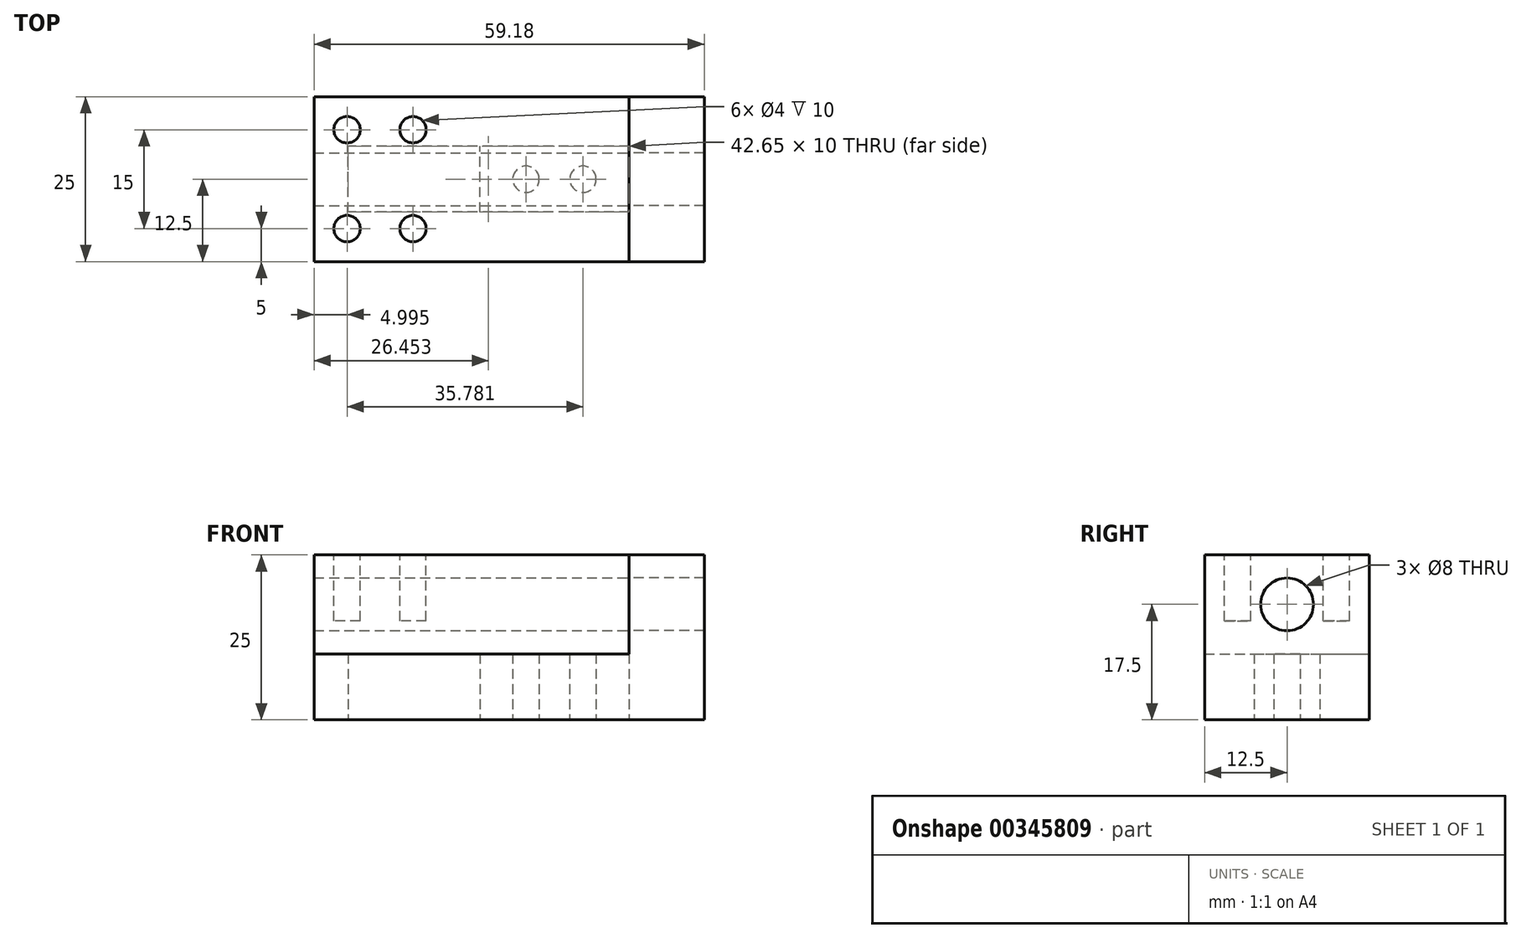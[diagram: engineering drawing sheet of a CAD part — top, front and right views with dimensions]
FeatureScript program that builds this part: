
annotation { "Feature Type Name" : "Feature", "Feature Type Description" : "" }
export const myFeature = defineFeature(function(context is Context, id is Id, definition is map)
    precondition{}
    {
        {
            var Q0;
            Q0=qCreatedBy(makeId("Top.planeOp"),FACE);
            var sketch = newSketch(context, id + "F0", { "sketchPlane" : qUnion([Q0])});
            skLineSegment(sketch, "E0.bottom", {"start": v(29.6, -12.5) * mm, "end": v(-29.6, -12.5) * mm});
            skLineSegment(sketch, "E0.top", {"start": v(29.6, 12.5) * mm, "end": v(-29.6, 12.5) * mm});
            skLineSegment(sketch, "E0.left", {"start": v(29.6, -12.5) * mm, "end": v(29.6, 12.5) * mm});
            skLineSegment(sketch, "E0.right", {"start": v(-29.6, -12.5) * mm, "end": v(-29.6, 12.5) * mm});
            skPoint(sketch, "E0.middle", {"position": v(0, 0) * mm});
            skLineSegment(sketch, "E1.bottom", {"start": v(24.46, -5) * mm, "end": v(-24.46, -5) * mm});
            skLineSegment(sketch, "E1.top", {"start": v(24.46, 5) * mm, "end": v(-24.46, 5) * mm});
            skLineSegment(sketch, "E1.left", {"start": v(24.46, -5) * mm, "end": v(24.46, 5) * mm});
            skLineSegment(sketch, "E1.right", {"start": v(-24.46, -5) * mm, "end": v(-24.46, 5) * mm});
            skSolve(sketch);
        }
        {
            var Q0;
            Q0 = qSketchRegion(id + "F0", true);
            extrude(context, id + "F1", {"entities" : qUnion([Q0]), "depth" : 10 * mm});
        }
        {
            var Q0;
            Q0=makeQuery(id+"F1.opExtrude","CAP_FACE",FACE,{"disambiguationData":[OSD([sQuery(id+"F0.wireOp",EDGE,"E0.bottom"),sQuery(id+"F0.wireOp",EDGE,"E0.top"),sQuery(id+"F0.wireOp",EDGE,"E0.left"),sQuery(id+"F0.wireOp",EDGE,"E0.right"),sQuery(id+"F0.wireOp",EDGE,"E1.bottom"),sQuery(id+"F0.wireOp",EDGE,"E1.top"),sQuery(id+"F0.wireOp",EDGE,"E1.left"),sQuery(id+"F0.wireOp",EDGE,"E1.right")])],"isStart":false});
            var sketch = newSketch(context, id + "F2", { "sketchPlane" : qUnion([Q0])});
            skLineSegment(sketch, "E2.bottom", {"start": v(29.6, -12.5) * mm, "end": v(18.19, -12.5) * mm});
            skLineSegment(sketch, "E2.top", {"start": v(29.6, 12.5) * mm, "end": v(18.19, 12.5) * mm});
            skLineSegment(sketch, "E2.left", {"start": v(29.6, -12.5) * mm, "end": v(29.6, 12.5) * mm});
            skLineSegment(sketch, "E2.right", {"start": v(18.19, -12.5) * mm, "end": v(18.19, 12.5) * mm});
            skSolve(sketch);
        }
        {
            var Q0;
            Q0 = qSketchRegion(id + "F2", true);
            extrude(context, id + "F3", {"entities" : qUnion([Q0]), "operationType" : NewBodyOperationType.ADD, "depth" : 15 * mm});
        }
        {
            var Q0;
            Q0 = qSketchRegion(id + "F2", true);
            extrude(context, id + "F4", {"entities" : qUnion([Q0]), "operationType" : NewBodyOperationType.ADD, "oppositeDirection" : true, "depth" : 10 * mm});
        }
        {
            var Q0;
            {var subQ0=sQuery(id+"F2.wireOp",EDGE,"E2.right");Q0=makeQuery(id+"F4.boolean.opBoolean","MERGE",FACE,{"derivedFrom":[makeQuery(id+"F3.opExtrude","SWEPT_FACE",FACE,{"disambiguationData":[OSD([subQ0])]}),makeQuery(id+"F4.opExtrude","SWEPT_FACE",FACE,{"disambiguationData":[OSD([subQ0])]})]});}
            var sketch = newSketch(context, id + "F5", { "sketchPlane" : qUnion([Q0])});
            skLineSegment(sketch, "E3", {"start": v(-12.5, 10) * mm, "end": v(12.5, 25) * mm, "construction": true});
            skCircle(sketch, "E4", {"center": v(0, 17.5) * mm, "radius": 4 * mm});
            skSolve(sketch);
        }
        {
            var Q0;
            Q0 = qSketchRegion(id + "F5", true);
            extrude(context, id + "F6", {"entities" : qUnion([Q0]), "operationType" : NewBodyOperationType.REMOVE, "oppositeDirection" : true, "depth" : 25 * mm});
        }
        {
            var Q0;
            Q0=makeQuery(id+"F1.opExtrude","SWEPT_BODY",BODY,{"disambiguationData":[OSD([sQuery(id+"F0.wireOp",EDGE,"E0.bottom"),sQuery(id+"F0.wireOp",EDGE,"E0.top"),sQuery(id+"F0.wireOp",EDGE,"E0.left"),sQuery(id+"F0.wireOp",EDGE,"E0.right"),sQuery(id+"F0.wireOp",EDGE,"E1.bottom"),sQuery(id+"F0.wireOp",EDGE,"E1.top"),sQuery(id+"F0.wireOp",EDGE,"E1.left"),sQuery(id+"F0.wireOp",EDGE,"E1.right")])]});
            transform(context, id + "F7", {"entities" : qUnion([Q0]), "transformType" : TransformType.TRANSLATION_3D, "dx" : 0 * mm, "dy" : 0 * mm, "dz" : 0 * mm, "makeCopy" : true});
        }
        {
            var Q0;
            Q0=makeQuery(id+"F7.opPattern","COPY",FACE,{"derivedFrom":makeQuery(id+"F4.boolean.opBoolean","MERGE",FACE,{"derivedFrom":[makeQuery(id+"F1.opExtrude","CAP_FACE",FACE,{"disambiguationData":[OSD([sQuery(id+"F0.wireOp",EDGE,"E0.bottom"),sQuery(id+"F0.wireOp",EDGE,"E0.top"),sQuery(id+"F0.wireOp",EDGE,"E0.left"),sQuery(id+"F0.wireOp",EDGE,"E0.right"),sQuery(id+"F0.wireOp",EDGE,"E1.bottom"),sQuery(id+"F0.wireOp",EDGE,"E1.top"),sQuery(id+"F0.wireOp",EDGE,"E1.left"),sQuery(id+"F0.wireOp",EDGE,"E1.right")])],"isStart":true}),makeQuery(id+"F4.opExtrude","CAP_FACE",FACE,{"disambiguationData":[OSD([sQuery(id+"F2.wireOp",EDGE,"E2.bottom"),sQuery(id+"F2.wireOp",EDGE,"E2.top"),sQuery(id+"F2.wireOp",EDGE,"E2.left"),sQuery(id+"F2.wireOp",EDGE,"E2.right")])],"isStart":false})]}),"instanceName":"1"});
            var sketch = newSketch(context, id + "F8", { "sketchPlane" : qUnion([Q0])});
            skLineSegment(sketch, "E5.bottom", {"start": v(-24.46, -5) * mm, "end": v(18.19, -5) * mm});
            skLineSegment(sketch, "E5.top", {"start": v(-24.46, 5) * mm, "end": v(18.19, 5) * mm});
            skLineSegment(sketch, "E5.left", {"start": v(-24.46, -5) * mm, "end": v(-24.46, 5) * mm});
            skLineSegment(sketch, "E5.right", {"start": v(18.19, -5) * mm, "end": v(18.19, 5) * mm});
            skSolve(sketch);
        }
        {
            var Q0;
            Q0 = qSketchRegion(id + "F8", true);
            extrude(context, id + "F9", {"entities" : qUnion([Q0]), "oppositeDirection" : true, "depth" : 10 * mm});
        }
        {
            var Q0;
            Q0=makeQuery(id+"F7.opPattern","COPY",FACE,{"derivedFrom":makeQuery(id+"F1.opExtrude","CAP_FACE",FACE,{"disambiguationData":[OSD([sQuery(id+"F0.wireOp",EDGE,"E0.bottom"),sQuery(id+"F0.wireOp",EDGE,"E0.top"),sQuery(id+"F0.wireOp",EDGE,"E0.left"),sQuery(id+"F0.wireOp",EDGE,"E0.right"),sQuery(id+"F0.wireOp",EDGE,"E1.bottom"),sQuery(id+"F0.wireOp",EDGE,"E1.top"),sQuery(id+"F0.wireOp",EDGE,"E1.left"),sQuery(id+"F0.wireOp",EDGE,"E1.right")])],"isStart":false}),"instanceName":"1"});
            var sketch = newSketch(context, id + "F10", { "sketchPlane" : qUnion([Q0])});
            skSolve(sketch);
        }
        {
            var Q0;
            {var subQ3=sQuery(id+"F0.wireOp",EDGE,"E0.right");Q0=makeQuery(id+"F10.imprint","IMPRINT",FACE,{"disambiguationData":[TD([[makeQuery(id+"F10.imprint","IMPRINT",EDGE,{"derivedFrom":makeQuery(id+"F7.opPattern","COPY",EDGE,{"derivedFrom":makeQuery(id+"F1.opExtrude","CAP_EDGE",EDGE,{"disambiguationData":[OSD([subQ3])],"isStart":false}),"instanceName":"1"})}),-1.0]])]});}
            var sketch = newSketch(context, id + "F11", { "sketchPlane" : qUnion([Q0])});
            skLineSegment(sketch, "E6.bottom", {"start": v(18.19, 12.5) * mm, "end": v(-29.6, 12.5) * mm});
            skLineSegment(sketch, "E6.top", {"start": v(18.19, -12.5) * mm, "end": v(-29.6, -12.5) * mm});
            skLineSegment(sketch, "E6.left", {"start": v(18.19, 12.5) * mm, "end": v(18.19, -12.5) * mm});
            skLineSegment(sketch, "E6.right", {"start": v(-29.6, 12.5) * mm, "end": v(-29.6, -12.5) * mm});
            skSolve(sketch);
        }
        {
            var Q0;
            Q0 = qSketchRegion(id + "F11", true);
            extrude(context, id + "F12", {"entities" : qUnion([Q0]), "depth" : 15 * mm});
        }
        {
            var Q0;
            Q0=makeQuery(id+"F9.opExtrude","SWEPT_BODY",BODY,{"disambiguationData":[OSD([sQuery(id+"F8.wireOp",EDGE,"E5.bottom"),sQuery(id+"F8.wireOp",EDGE,"E5.top"),sQuery(id+"F8.wireOp",EDGE,"E5.left"),sQuery(id+"F8.wireOp",EDGE,"E5.right")])]});
            var Q1;
            Q1=makeQuery(id+"F12.opExtrude","SWEPT_BODY",BODY,{"disambiguationData":[OSD([sQuery(id+"F11.wireOp",EDGE,"E6.bottom"),sQuery(id+"F11.wireOp",EDGE,"E6.top"),sQuery(id+"F11.wireOp",EDGE,"E6.left"),sQuery(id+"F11.wireOp",EDGE,"E6.right")])]});
            booleanBodies(context, id + "F13", {"operationType" : BooleanOperationType.UNION, "tools" : qUnion([Q0, Q1])});
        }
        {
            var Q0;
            Q0=makeQuery(id+"F13.opBoolean","MERGE",FACE,{"derivedFrom":[makeQuery(id+"F9.opExtrude","SWEPT_FACE",FACE,{"disambiguationData":[OSD([sQuery(id+"F8.wireOp",EDGE,"E5.right")])]}),makeQuery(id+"F12.opExtrude","SWEPT_FACE",FACE,{"disambiguationData":[OSD([sQuery(id+"F11.wireOp",EDGE,"E6.left")])]})]});
            var sketch = newSketch(context, id + "F14", { "sketchPlane" : qUnion([Q0])});
            skLineSegment(sketch, "E7", {"start": v(-12.5, 25) * mm, "end": v(12.5, 10) * mm, "construction": true});
            skCircle(sketch, "E8", {"center": v(0, 17.5) * mm, "radius": 4 * mm});
            skSolve(sketch);
        }
        {
            var Q0;
            Q0 = qSketchRegion(id + "F14", true);
            extrude(context, id + "F15", {"entities" : qUnion([Q0]), "operationType" : NewBodyOperationType.REMOVE, "endBound" : BoundingType.THROUGH_ALL, "oppositeDirection" : true, "depth" : 25 * mm});
        }
        {
            var Q0;
            Q0=makeQuery(id+"F9.opExtrude","CAP_FACE",FACE,{"disambiguationData":[OSD([sQuery(id+"F8.wireOp",EDGE,"E5.bottom"),sQuery(id+"F8.wireOp",EDGE,"E5.top"),sQuery(id+"F8.wireOp",EDGE,"E5.left"),sQuery(id+"F8.wireOp",EDGE,"E5.right")])],"isStart":true});
            var sketch = newSketch(context, id + "F16", { "sketchPlane" : qUnion([Q0])});
            skLineSegment(sketch, "E9.bottom", {"start": v(-24.46, 5) * mm, "end": v(-4.46, 5) * mm});
            skLineSegment(sketch, "E9.top", {"start": v(-24.46, -5) * mm, "end": v(-4.46, -5) * mm});
            skLineSegment(sketch, "E9.left", {"start": v(-24.46, 5) * mm, "end": v(-24.46, -5) * mm});
            skLineSegment(sketch, "E9.right", {"start": v(-4.46, 5) * mm, "end": v(-4.46, -5) * mm});
            skLineSegment(sketch, "E10", {"start": v(-4.46, 0) * mm, "end": v(18.19, 0) * mm, "construction": true});
            skCircle(sketch, "E11", {"center": v(11.19, 0) * mm, "radius": 2 * mm});
            skCircle(sketch, "E12", {"center": v(2.54, 0) * mm, "radius": 2 * mm});
            skPoint(sketch, "E13", {"position": v(6.86, 0) * mm});
            skSolve(sketch);
        }
        {
            var Q0;
            Q0 = qSketchRegion(id + "F16", true);
            extrude(context, id + "F17", {"entities" : qUnion([Q0]), "operationType" : NewBodyOperationType.REMOVE, "oppositeDirection" : true, "depth" : 10 * mm});
        }
        {
            var Q0;
            Q0=makeQuery(id+"F12.opExtrude","CAP_FACE",FACE,{"disambiguationData":[OSD([sQuery(id+"F11.wireOp",EDGE,"E6.bottom"),sQuery(id+"F11.wireOp",EDGE,"E6.top"),sQuery(id+"F11.wireOp",EDGE,"E6.left"),sQuery(id+"F11.wireOp",EDGE,"E6.right")])],"isStart":false});
            var sketch = newSketch(context, id + "F18", { "sketchPlane" : qUnion([Q0])});
            skCircle(sketch, "E14", {"center": v(-24.6, 7.5) * mm, "radius": 2 * mm});
            skLineSegment(sketch, "E15", {"start": v(-29.6, 0) * mm, "end": v(18.19, 0) * mm, "construction": true});
            skCircle(sketch, "E16.MirrorC", {"center": v(-24.6, -7.5) * mm, "radius": 2 * mm});
            skLineSegment(sketch, "E17", {"start": v(-19.6, 12.5) * mm, "end": v(-19.6, -12.5) * mm, "construction": true});
            skCircle(sketch, "E18.MirrorC", {"center": v(-14.6, 7.5) * mm, "radius": 2 * mm});
            skCircle(sketch, "E19.MirrorC", {"center": v(-14.6, -7.5) * mm, "radius": 2 * mm});
            skSolve(sketch);
        }
        {
            var Q0;
            Q0 = qSketchRegion(id + "F18", true);
            extrude(context, id + "F19", {"entities" : qUnion([Q0]), "operationType" : NewBodyOperationType.REMOVE, "oppositeDirection" : true, "depth" : 10 * mm});
        }
    });
